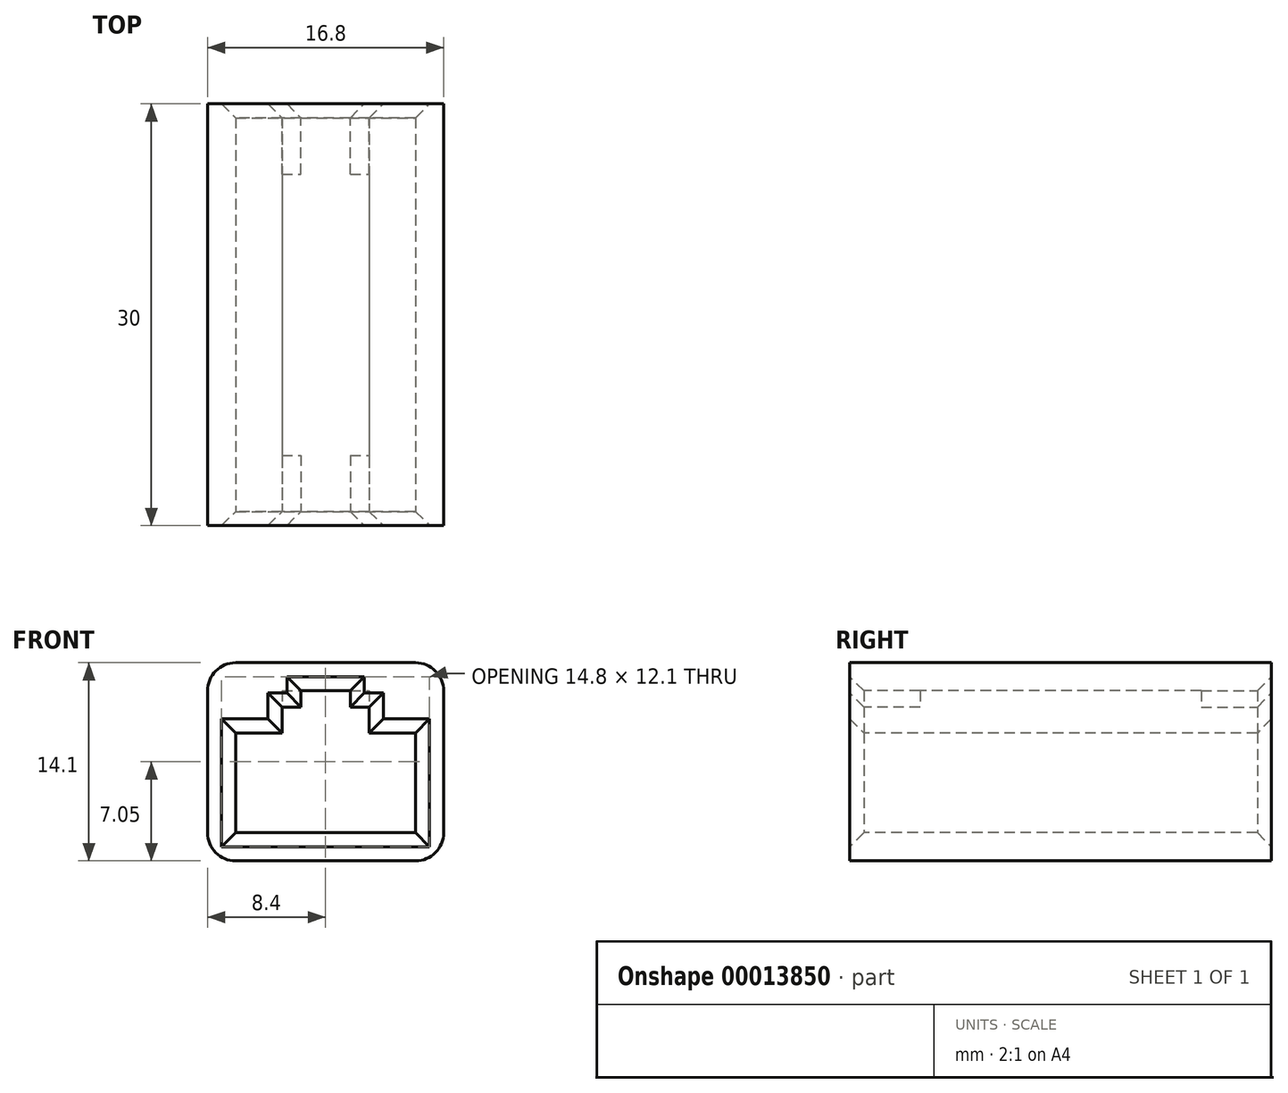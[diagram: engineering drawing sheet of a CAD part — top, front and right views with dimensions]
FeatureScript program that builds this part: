
annotation { "Feature Type Name" : "Feature", "Feature Type Description" : "" }
export const myFeature = defineFeature(function(context is Context, id is Id, definition is map)
    precondition{}
    {
        {
            var Q0;
            Q0=qCreatedBy(makeId("Front.planeOp"),FACE);
            var sketch = newSketch(context, id + "F0", { "sketchPlane" : qUnion([Q0])});
            skLineSegment(sketch, "E0.bottom", {"start": v(-6.4, 3.55) * mm, "end": v(6.4, 3.55) * mm});
            skLineSegment(sketch, "E0.top", {"start": v(-6.4, -3.55) * mm, "end": v(6.4, -3.55) * mm});
            skLineSegment(sketch, "E0.left", {"start": v(-6.4, 3.55) * mm, "end": v(-6.4, -3.55) * mm});
            skLineSegment(sketch, "E0.right", {"start": v(6.4, 3.55) * mm, "end": v(6.4, -3.55) * mm});
            skLineSegment(sketch, "E1", {"start": v(6.4, 3.55) * mm, "end": v(-6.4, -3.55) * mm, "construction": true});
            skLineSegment(sketch, "E2.bottom", {"start": v(-3.1, 6.55) * mm, "end": v(3.1, 6.55) * mm});
            skLineSegment(sketch, "E2.top", {"start": v(-3.1, 3.55) * mm, "end": v(3.1, 3.55) * mm});
            skLineSegment(sketch, "E2.left", {"start": v(-3.1, 6.55) * mm, "end": v(-3.1, 3.55) * mm});
            skLineSegment(sketch, "E2.right", {"start": v(3.1, 6.55) * mm, "end": v(3.1, 3.55) * mm});
            skPoint(sketch, "E3", {"position": v(0, 3.55) * mm});
            skLineSegment(sketch, "E4.bottom", {"start": v(-8.4, 8.55) * mm, "end": v(8.4, 8.55) * mm});
            skLineSegment(sketch, "E4.top", {"start": v(-8.4, -5.55) * mm, "end": v(8.4, -5.55) * mm});
            skLineSegment(sketch, "E4.left", {"start": v(-8.4, 8.55) * mm, "end": v(-8.4, -5.55) * mm});
            skLineSegment(sketch, "E4.right", {"start": v(8.4, 8.55) * mm, "end": v(8.4, -5.55) * mm});
            skLineSegment(sketch, "E5", {"start": v(-1.75, 6.55) * mm, "end": v(-1.75, 5.4) * mm});
            skLineSegment(sketch, "E6", {"start": v(-1.75, 5.4) * mm, "end": v(-3.1, 5.4) * mm});
            skLineSegment(sketch, "E7.MirrorCS", {"start": v(1.75, 6.55) * mm, "end": v(1.75, 5.4) * mm});
            skLineSegment(sketch, "E8.MirrorCS", {"start": v(1.75, 5.4) * mm, "end": v(3.1, 5.4) * mm});
            skSolve(sketch);
        }
        {
            var Q0;
            Q0=makeQuery(id+"F0.imprint","IMPRINT",FACE,{"disambiguationData":[TD([[makeQuery(id+"F0.imprint","IMPRINT",EDGE,{"derivedFrom":sQuery(id+"F0.wireOp",EDGE,"E0.top")}),-1.0]])]});
            extrude(context, id + "F1", {"entities" : qUnion([Q0]), "oppositeDirection" : true, "depth" : 15 * mm});
        }
        {
            var Q0;
            {var subQ1=sQuery(id+"F0.wireOp",EDGE,"E5");Q0=makeQuery(id+"F0.imprint","IMPRINT",FACE,{"disambiguationData":[TD([[makeQuery(id+"F0.imprint","IMPRINT",EDGE,{"derivedFrom":subQ1}),-1.0]])]});}
            var Q1;
            {var subQ4=sQuery(id+"F0.wireOp",EDGE,"E7.MirrorCS");Q1=makeQuery(id+"F0.imprint","IMPRINT",FACE,{"disambiguationData":[TD([[makeQuery(id+"F0.imprint","IMPRINT",EDGE,{"derivedFrom":subQ4}),1.0]])]});}
            extrude(context, id + "F2", {"entities" : qUnion([Q0, Q1]), "operationType" : NewBodyOperationType.ADD, "oppositeDirection" : true, "depth" : 5 * mm});
        }
        {
            var Q0;
            Q0=makeQuery(id+"F1.opExtrude","CAP_EDGE",EDGE,{"disambiguationData":[OSD([sQuery(id+"F0.wireOp",EDGE,"E0.right")])],"isStart":true});
            var Q1;
            {var subQ0=sQuery(id+"F0.wireOp",EDGE,"E0.bottom");Q1=makeQuery(id+"F1.opExtrude","CAP_EDGE",EDGE,{"disambiguationData":[OSD([subQ0]),TDD([makeQuery(id+"F0.imprint","IMPRINT",EDGE,{"disambiguationData":[TD([[makeQuery(id+"F0.imprint","INTERSECT",VERTEX,{"derivedFrom":[subQ0,sQuery(id+"F0.wireOp",EDGE,"E0.right")]}),1.0]])],"derivedFrom":subQ0})])],"isStart":true});}
            var Q2;
            Q2=makeQuery(id+"F1.opExtrude","CAP_EDGE",EDGE,{"disambiguationData":[OSD([sQuery(id+"F0.wireOp",EDGE,"E2.right")])],"isStart":true});
            var Q3;
            Q3=makeQuery(id+"F2.opExtrude","CAP_EDGE",EDGE,{"disambiguationData":[OSD([sQuery(id+"F0.wireOp",EDGE,"E8.MirrorCS")])],"isStart":true});
            var Q4;
            Q4=makeQuery(id+"F2.opExtrude","CAP_EDGE",EDGE,{"disambiguationData":[OSD([sQuery(id+"F0.wireOp",EDGE,"E7.MirrorCS")])],"isStart":true});
            var Q5;
            Q5=makeQuery(id+"F1.opExtrude","CAP_EDGE",EDGE,{"disambiguationData":[OSD([sQuery(id+"F0.wireOp",EDGE,"E2.bottom")])],"isStart":true});
            var Q6;
            Q6=makeQuery(id+"F2.opExtrude","CAP_EDGE",EDGE,{"disambiguationData":[OSD([sQuery(id+"F0.wireOp",EDGE,"E5")])],"isStart":true});
            var Q7;
            Q7=makeQuery(id+"F2.opExtrude","CAP_EDGE",EDGE,{"disambiguationData":[OSD([sQuery(id+"F0.wireOp",EDGE,"E6")])],"isStart":true});
            var Q8;
            Q8=makeQuery(id+"F1.opExtrude","CAP_EDGE",EDGE,{"disambiguationData":[OSD([sQuery(id+"F0.wireOp",EDGE,"E2.left")])],"isStart":true});
            var Q9;
            {var subQ0=sQuery(id+"F0.wireOp",EDGE,"E0.bottom");Q9=makeQuery(id+"F1.opExtrude","CAP_EDGE",EDGE,{"disambiguationData":[OSD([subQ0]),TDD([makeQuery(id+"F0.imprint","IMPRINT",EDGE,{"disambiguationData":[TD([[makeQuery(id+"F0.imprint","INTERSECT",VERTEX,{"derivedFrom":[subQ0,sQuery(id+"F0.wireOp",EDGE,"E0.left")]}),-1.0]])],"derivedFrom":subQ0})])],"isStart":true});}
            var Q10;
            Q10=makeQuery(id+"F1.opExtrude","CAP_EDGE",EDGE,{"disambiguationData":[OSD([sQuery(id+"F0.wireOp",EDGE,"E0.left")])],"isStart":true});
            var Q11;
            Q11=makeQuery(id+"F1.opExtrude","CAP_EDGE",EDGE,{"disambiguationData":[OSD([sQuery(id+"F0.wireOp",EDGE,"E0.top")])],"isStart":true});
            chamfer(context, id + "F3", {"entities" : qUnion([Q0, Q1, Q2, Q3, Q4, Q5, Q6, Q7, Q8, Q9, Q10, Q11]), "width" : 1 * mm, "tangentPropagation" : true});
        }
        {
            var Q0;
            Q0=makeQuery(id+"F1.opExtrude","SWEPT_BODY",BODY,{"disambiguationData":[OSD([sQuery(id+"F0.wireOp",EDGE,"E0.bottom"),sQuery(id+"F0.wireOp",EDGE,"E0.top"),sQuery(id+"F0.wireOp",EDGE,"E0.left"),sQuery(id+"F0.wireOp",EDGE,"E0.right"),sQuery(id+"F0.wireOp",EDGE,"E2.bottom"),sQuery(id+"F0.wireOp",EDGE,"E2.left"),sQuery(id+"F0.wireOp",EDGE,"E2.right"),sQuery(id+"F0.wireOp",EDGE,"E4.bottom"),sQuery(id+"F0.wireOp",EDGE,"E4.top"),sQuery(id+"F0.wireOp",EDGE,"E4.left"),sQuery(id+"F0.wireOp",EDGE,"E4.right")])]});
            var Q1;
            Q1=makeQuery(id+"F1.opExtrude","CAP_FACE",FACE,{"disambiguationData":[OSD([sQuery(id+"F0.wireOp",EDGE,"E0.bottom"),sQuery(id+"F0.wireOp",EDGE,"E0.top"),sQuery(id+"F0.wireOp",EDGE,"E0.left"),sQuery(id+"F0.wireOp",EDGE,"E0.right"),sQuery(id+"F0.wireOp",EDGE,"E2.bottom"),sQuery(id+"F0.wireOp",EDGE,"E2.left"),sQuery(id+"F0.wireOp",EDGE,"E2.right"),sQuery(id+"F0.wireOp",EDGE,"E4.bottom"),sQuery(id+"F0.wireOp",EDGE,"E4.top"),sQuery(id+"F0.wireOp",EDGE,"E4.left"),sQuery(id+"F0.wireOp",EDGE,"E4.right")])],"isStart":false});
            mirror(context, id + "F4", {"operationType" : NewBodyOperationType.ADD, "entities" : qUnion([Q0]), "mirrorPlane" : qUnion([Q1])});
        }
        {
            var Q0;
            {var subQ0=makeQuery(id+"F1.opExtrude","SWEPT_EDGE",EDGE,{"disambiguationData":[OSD([sQuery(id+"F0.wireOp",EDGE,"E4.bottom"),sQuery(id+"F0.wireOp",EDGE,"E4.left")])]});Q0=makeQuery(id+"F4.boolean.opBoolean","MERGE",EDGE,{"derivedFrom":[subQ0,makeQuery(id+"F4.opPattern","COPY",EDGE,{"derivedFrom":subQ0,"instanceName":"1"})]});}
            var Q1;
            {var subQ0=makeQuery(id+"F1.opExtrude","SWEPT_EDGE",EDGE,{"disambiguationData":[OSD([sQuery(id+"F0.wireOp",EDGE,"E4.top"),sQuery(id+"F0.wireOp",EDGE,"E4.left")])]});Q1=makeQuery(id+"F4.boolean.opBoolean","MERGE",EDGE,{"derivedFrom":[subQ0,makeQuery(id+"F4.opPattern","COPY",EDGE,{"derivedFrom":subQ0,"instanceName":"1"})]});}
            var Q2;
            {var subQ0=makeQuery(id+"F1.opExtrude","SWEPT_EDGE",EDGE,{"disambiguationData":[OSD([sQuery(id+"F0.wireOp",EDGE,"E4.top"),sQuery(id+"F0.wireOp",EDGE,"E4.right")])]});Q2=makeQuery(id+"F4.boolean.opBoolean","MERGE",EDGE,{"derivedFrom":[subQ0,makeQuery(id+"F4.opPattern","COPY",EDGE,{"derivedFrom":subQ0,"instanceName":"1"})]});}
            var Q3;
            {var subQ0=makeQuery(id+"F1.opExtrude","SWEPT_EDGE",EDGE,{"disambiguationData":[OSD([sQuery(id+"F0.wireOp",EDGE,"E4.bottom"),sQuery(id+"F0.wireOp",EDGE,"E4.right")])]});Q3=makeQuery(id+"F4.boolean.opBoolean","MERGE",EDGE,{"derivedFrom":[subQ0,makeQuery(id+"F4.opPattern","COPY",EDGE,{"derivedFrom":subQ0,"instanceName":"1"})]});}
            fillet(context, id + "F5", {"entities" : qUnion([Q0, Q1, Q2, Q3]), "radius" : 2 * mm, "tangentPropagation" : true, "allowEdgeOverflow" : false});
        }
    });
